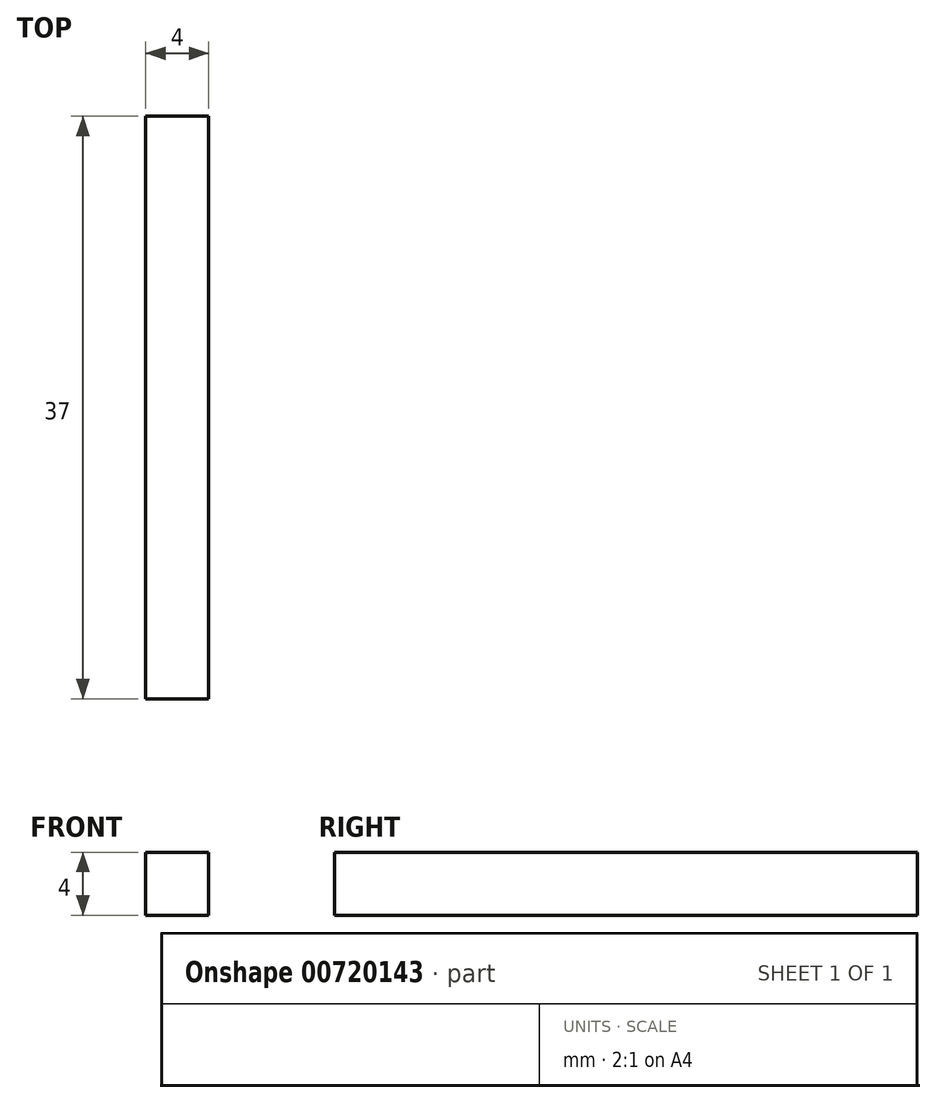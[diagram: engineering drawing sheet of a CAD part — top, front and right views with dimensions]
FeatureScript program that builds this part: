
annotation { "Feature Type Name" : "Feature", "Feature Type Description" : "" }
export const myFeature = defineFeature(function(context is Context, id is Id, definition is map)
    precondition{}
    {
        {
            var Q0;
            Q0=qCreatedBy(makeId("Front.planeOp"),FACE);
            var sketch = newSketch(context, id + "F0", { "sketchPlane" : qUnion([Q0])});
            skLineSegment(sketch, "E0.bottom", {"start": v(0, 0) * mm, "end": v(4, 0) * mm});
            skLineSegment(sketch, "E0.top", {"start": v(0, 4) * mm, "end": v(4, 4) * mm});
            skLineSegment(sketch, "E0.left", {"start": v(0, 0) * mm, "end": v(0, 4) * mm});
            skLineSegment(sketch, "E0.right", {"start": v(4, 0) * mm, "end": v(4, 4) * mm});
            skSolve(sketch);
        }
        {
            var Q0;
            Q0=makeQuery(id+"F0.imprint","IMPRINT",FACE,{"disambiguationData":[TD([[makeQuery(id+"F0.imprint","IMPRINT",EDGE,{"derivedFrom":sQuery(id+"F0.wireOp",EDGE,"E0.bottom")}),1.0]])]});
            extrude(context, id + "F1", {"entities" : qUnion([Q0]), "depth" : 37 * mm, "offsetDistance" : 25 * mm});
        }
    });
